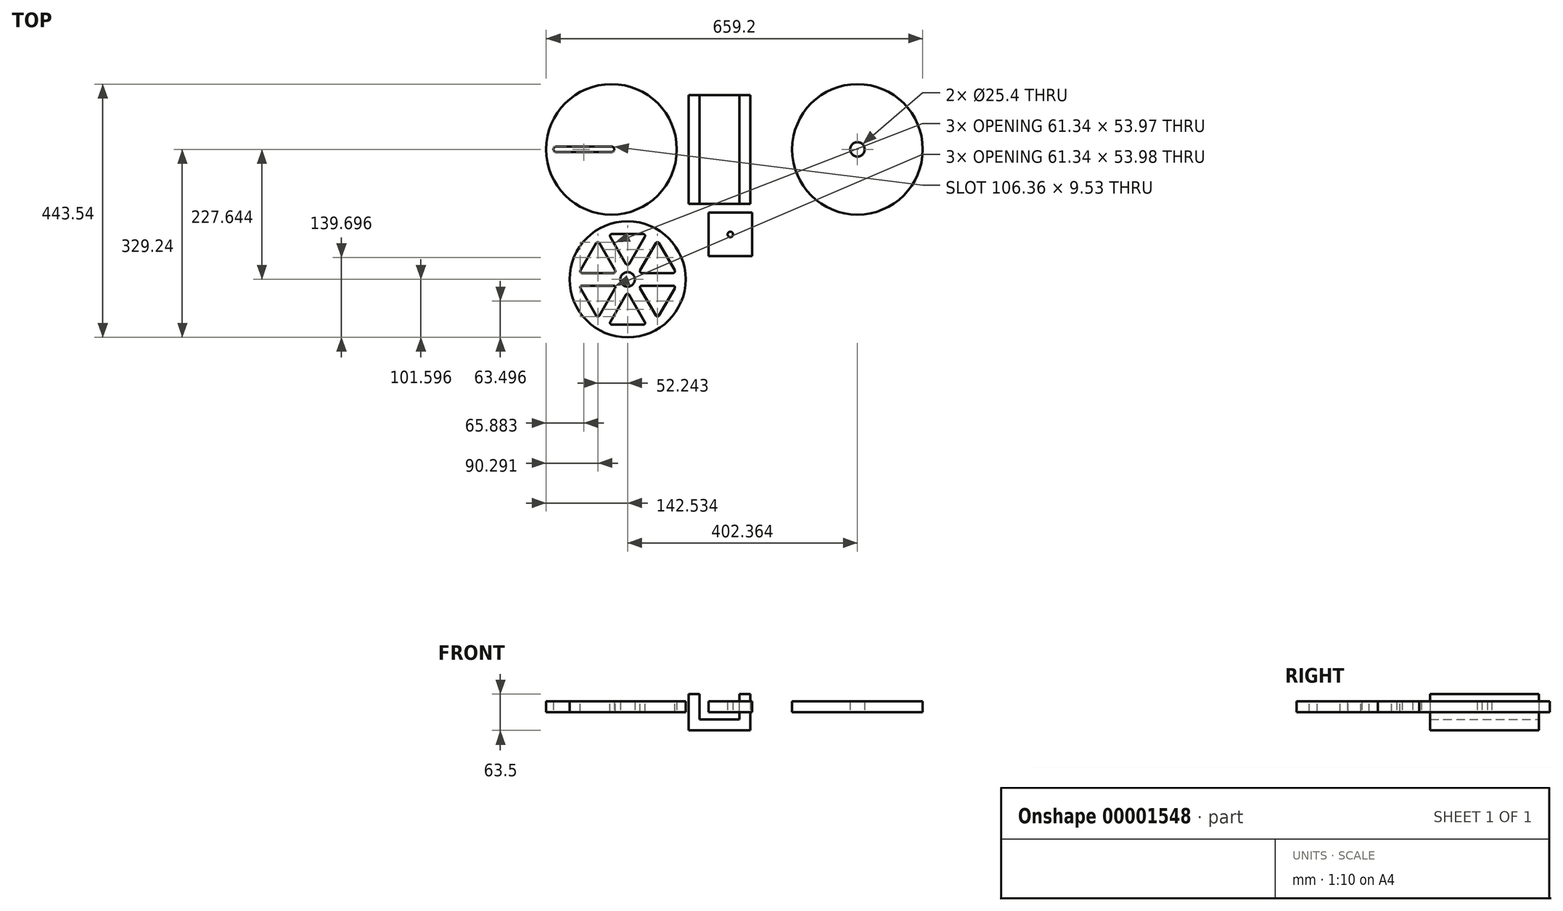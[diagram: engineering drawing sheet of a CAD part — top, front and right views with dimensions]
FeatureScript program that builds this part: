
annotation { "Feature Type Name" : "Feature", "Feature Type Description" : "" }
export const myFeature = defineFeature(function(context is Context, id is Id, definition is map)
    precondition{}
    {
        {
            var Q0;
            Q0=qCreatedBy(makeId("Front.planeOp"),FACE);
            var sketch = newSketch(context, id + "F0", { "sketchPlane" : qUnion([Q0])});
            skLineSegment(sketch, "E0.bottom", {"start": v(-53.98, 31.75) * mm, "end": v(-34.92, 31.75) * mm});
            skLineSegment(sketch, "E0.top", {"start": v(-53.97, -31.75) * mm, "end": v(53.98, -31.75) * mm});
            skLineSegment(sketch, "E0.left", {"start": v(-53.98, 31.75) * mm, "end": v(-53.98, -31.75) * mm});
            skLineSegment(sketch, "E0.right", {"start": v(53.98, 31.75) * mm, "end": v(53.98, -31.75) * mm});
            skLineSegment(sketch, "E1.0", {"start": v(-34.92, 12.7) * mm, "end": v(-34.92, -12.7) * mm});
            skLineSegment(sketch, "E1.2", {"start": v(34.93, 12.7) * mm, "end": v(34.93, -12.7) * mm});
            skLineSegment(sketch, "E1.3", {"start": v(-34.92, -12.7) * mm, "end": v(34.93, -12.7) * mm});
            skLineSegment(sketch, "E2", {"start": v(-34.92, 12.7) * mm, "end": v(-34.92, 31.75) * mm});
            skLineSegment(sketch, "E3", {"start": v(34.93, 12.7) * mm, "end": v(34.93, 31.75) * mm});
            skLineSegment(sketch, "E4.trimOffspring", {"start": v(34.93, 31.75) * mm, "end": v(53.98, 31.75) * mm});
            skSolve(sketch);
        }
        {
            var Q0;
            Q0=makeQuery(id+"F0.imprint","IMPRINT",FACE,{"disambiguationData":[TD([[makeQuery(id+"F0.imprint","IMPRINT",EDGE,{"derivedFrom":sQuery(id+"F0.wireOp",EDGE,"E0.bottom")}),-1.0]])]});
            extrude(context, id + "F1", {"entities" : qUnion([Q0]), "endBound" : BoundingType.SYMMETRIC, "depth" : 190.5 * mm});
        }
        {
            var Q0;
            Q0=qCreatedBy(makeId("Top.planeOp"),FACE);
            var sketch = newSketch(context, id + "F2", { "sketchPlane" : qUnion([Q0])});
            skCircle(sketch, "E5", {"center": v(241.4, 0) * mm, "radius": 114.3 * mm});
            skCircle(sketch, "E6", {"center": v(-189.19, 0) * mm, "radius": 114.3 * mm});
            skCircle(sketch, "E7", {"center": v(241.4, 0) * mm, "radius": 12.7 * mm});
            skArc(sketch, "E8", {"start": v(-189.19, -4.76) * mm, "mid": v(-184.43, 0) * mm, "end": v(-189.19, 4.76) * mm});
            skArc(sketch, "E9", {"start": v(-286.03, 4.76) * mm, "mid": v(-290.79, 0) * mm, "end": v(-286.03, -4.76) * mm});
            skLineSegment(sketch, "E10", {"start": v(-286.03, 4.76) * mm, "end": v(-189.19, 4.76) * mm});
            skLineSegment(sketch, "E11", {"start": v(-189.19, -4.76) * mm, "end": v(-286.03, -4.76) * mm});
            skLineSegment(sketch, "E12.bottom", {"start": v(-19.25, -110.9) * mm, "end": v(56.95, -110.9) * mm});
            skLineSegment(sketch, "E12.top", {"start": v(-19.25, -187.1) * mm, "end": v(56.95, -187.1) * mm});
            skLineSegment(sketch, "E12.left", {"start": v(-19.25, -110.9) * mm, "end": v(-19.25, -187.1) * mm});
            skLineSegment(sketch, "E12.right", {"start": v(56.95, -110.9) * mm, "end": v(56.95, -187.1) * mm});
            skCircle(sketch, "E13", {"center": v(18.85, -149) * mm, "radius": 4.76 * mm});
            skCircle(sketch, "E14", {"center": v(-160.96, -227.64) * mm, "radius": 101.6 * mm});
            skCircle(sketch, "E15", {"center": v(-160.96, -227.64) * mm, "radius": 12.7 * mm});
            skSolve(sketch);
        }
        {
            var Q0;
            {Q0=qUnion([makeQuery(id+"F2.imprint","IMPRINT",FACE,{"disambiguationData":[TD([[makeQuery(id+"F2.imprint","IMPRINT",EDGE,{"derivedFrom":sQuery(id+"F2.wireOp",EDGE,"E5")}),1.0]])]}),makeQuery(id+"F2.imprint","IMPRINT",FACE,{"disambiguationData":[TD([[makeQuery(id+"F2.imprint","IMPRINT",EDGE,{"derivedFrom":sQuery(id+"F2.wireOp",EDGE,"E6")}),1.0]])]}),makeQuery(id+"F2.imprint","IMPRINT",FACE,{"disambiguationData":[TD([[makeQuery(id+"F2.imprint","IMPRINT",EDGE,{"derivedFrom":sQuery(id+"F2.wireOp",EDGE,"E12.bottom")}),-1.0]])]}),makeQuery(id+"F2.imprint","IMPRINT",FACE,{"disambiguationData":[TD([[makeQuery(id+"F2.imprint","IMPRINT",EDGE,{"derivedFrom":sQuery(id+"F2.wireOp",EDGE,"E14")}),1.0]])]})]);}
            extrude(context, id + "F3", {"entities" : qUnion([Q0]), "depth" : 19.05 * mm});
        }
        {
            var Q0;
            Q0=makeQuery(id+"F3.opExtrude","CAP_FACE",FACE,{"disambiguationData":[OSD([sQuery(id+"F2.wireOp",EDGE,"E14"),sQuery(id+"F2.wireOp",EDGE,"E15")])],"isStart":false});
            var sketch = newSketch(context, id + "F4", { "sketchPlane" : qUnion([Q0])});
            skLineSegment(sketch, "E16", {"start": v(-160.96, -227.64) * mm, "end": v(-160.96, -126.04) * mm, "construction": true});
            skLineSegment(sketch, "E17", {"start": v(-160.96, -227.64) * mm, "end": v(-59.36, -227.64) * mm});
            skCircle(sketch, "E18.cCircle", {"center": v(-160.96, -167.32) * mm, "radius": 19.05 * mm, "construction": true});
            skLineSegment(sketch, "E18.0", {"start": v(-188.45, -148.27) * mm, "end": v(-133.46, -148.27) * mm});
            skLineSegment(sketch, "E18.1", {"start": v(-130.71, -153.03) * mm, "end": v(-158.2, -200.66) * mm});
            skLineSegment(sketch, "E18.2", {"start": v(-163.7, -200.66) * mm, "end": v(-191.2, -153.03) * mm});
            skPoint(sketch, "E18.0.midPoint", {"position": v(-160.96, -148.27) * mm});
            skPoint(sketch, "E19.visualSharp", {"position": v(-193.95, -148.27) * mm});
            skArc(sketch, "E19.filletArc", {"start": v(-188.45, -148.27) * mm, "mid": v(-191.2, -149.86) * mm, "end": v(-191.2, -153.03) * mm});
            skPoint(sketch, "E20.visualSharp", {"position": v(-160.96, -205.42) * mm});
            skArc(sketch, "E20.filletArc", {"start": v(-163.7, -200.66) * mm, "mid": v(-160.96, -202.24) * mm, "end": v(-158.2, -200.66) * mm});
            skPoint(sketch, "E21.visualSharp", {"position": v(-127.96, -148.27) * mm});
            skArc(sketch, "E21.filletArc", {"start": v(-130.71, -153.03) * mm, "mid": v(-130.71, -149.86) * mm, "end": v(-133.46, -148.27) * mm});
            skSolve(sketch);
        }
        {
            var Q0;
            Q0=makeQuery(id+"F4.imprint","IMPRINT",FACE,{"disambiguationData":[TD([[makeQuery(id+"F4.imprint","IMPRINT",EDGE,{"derivedFrom":sQuery(id+"F4.wireOp",EDGE,"E18.0")}),-1.0]])]});
            extrude(context, id + "F5", {"entities" : qUnion([Q0]), "oppositeDirection" : true, "depth" : 19.05 * mm});
        }
        {
            var Q0;
            Q0=makeQuery(id+"F3.opExtrude","CAP_FACE",FACE,{"disambiguationData":[OSD([sQuery(id+"F2.wireOp",EDGE,"E14"),sQuery(id+"F2.wireOp",EDGE,"E15")])],"isStart":false});
            var Q1;
            Q1=makeQuery(id+"F5.opExtrude","SWEPT_BODY",BODY,{"disambiguationData":[OSD([sQuery(id+"F4.wireOp",EDGE,"E18.0"),sQuery(id+"F4.wireOp",EDGE,"E18.1"),sQuery(id+"F4.wireOp",EDGE,"E18.2"),sQuery(id+"F4.wireOp",EDGE,"E19.filletArc"),sQuery(id+"F4.wireOp",EDGE,"E20.filletArc"),sQuery(id+"F4.wireOp",EDGE,"E21.filletArc")])]});
            var Q2;
            Q2=makeQuery(id+"F3.opExtrude","CAP_EDGE",EDGE,{"disambiguationData":[OSD([sQuery(id+"F2.wireOp",EDGE,"E15")])],"isStart":false});
            circularPattern(context, id + "F6", {"entities" : qUnion([Q1]), "axis" : qUnion([Q2]), "angle" : 360 * degree, "instanceCount" : 6, "equalSpace" : true});
        }
        {
            var Q0;
            Q0=makeQuery(id+"F6.opPattern","COPY",BODY,{"derivedFrom":makeQuery(id+"F5.opExtrude","SWEPT_BODY",BODY,{"disambiguationData":[OSD([sQuery(id+"F4.wireOp",EDGE,"E18.0"),sQuery(id+"F4.wireOp",EDGE,"E18.1"),sQuery(id+"F4.wireOp",EDGE,"E18.2"),sQuery(id+"F4.wireOp",EDGE,"E19.filletArc"),sQuery(id+"F4.wireOp",EDGE,"E20.filletArc"),sQuery(id+"F4.wireOp",EDGE,"E21.filletArc")])]}),"instanceName":"1"});
            var Q1;
            Q1=makeQuery(id+"F5.opExtrude","SWEPT_BODY",BODY,{"disambiguationData":[OSD([sQuery(id+"F4.wireOp",EDGE,"E18.0"),sQuery(id+"F4.wireOp",EDGE,"E18.1"),sQuery(id+"F4.wireOp",EDGE,"E18.2"),sQuery(id+"F4.wireOp",EDGE,"E19.filletArc"),sQuery(id+"F4.wireOp",EDGE,"E20.filletArc"),sQuery(id+"F4.wireOp",EDGE,"E21.filletArc")])]});
            var Q2;
            Q2=makeQuery(id+"F6.opPattern","COPY",BODY,{"derivedFrom":makeQuery(id+"F5.opExtrude","SWEPT_BODY",BODY,{"disambiguationData":[OSD([sQuery(id+"F4.wireOp",EDGE,"E18.0"),sQuery(id+"F4.wireOp",EDGE,"E18.1"),sQuery(id+"F4.wireOp",EDGE,"E18.2"),sQuery(id+"F4.wireOp",EDGE,"E19.filletArc"),sQuery(id+"F4.wireOp",EDGE,"E20.filletArc"),sQuery(id+"F4.wireOp",EDGE,"E21.filletArc")])]}),"instanceName":"5"});
            var Q3;
            Q3=makeQuery(id+"F6.opPattern","COPY",BODY,{"derivedFrom":makeQuery(id+"F5.opExtrude","SWEPT_BODY",BODY,{"disambiguationData":[OSD([sQuery(id+"F4.wireOp",EDGE,"E18.0"),sQuery(id+"F4.wireOp",EDGE,"E18.1"),sQuery(id+"F4.wireOp",EDGE,"E18.2"),sQuery(id+"F4.wireOp",EDGE,"E19.filletArc"),sQuery(id+"F4.wireOp",EDGE,"E20.filletArc"),sQuery(id+"F4.wireOp",EDGE,"E21.filletArc")])]}),"instanceName":"4"});
            var Q4;
            Q4=makeQuery(id+"F6.opPattern","COPY",BODY,{"derivedFrom":makeQuery(id+"F5.opExtrude","SWEPT_BODY",BODY,{"disambiguationData":[OSD([sQuery(id+"F4.wireOp",EDGE,"E18.0"),sQuery(id+"F4.wireOp",EDGE,"E18.1"),sQuery(id+"F4.wireOp",EDGE,"E18.2"),sQuery(id+"F4.wireOp",EDGE,"E19.filletArc"),sQuery(id+"F4.wireOp",EDGE,"E20.filletArc"),sQuery(id+"F4.wireOp",EDGE,"E21.filletArc")])]}),"instanceName":"3"});
            var Q5;
            Q5=makeQuery(id+"F6.opPattern","COPY",BODY,{"derivedFrom":makeQuery(id+"F5.opExtrude","SWEPT_BODY",BODY,{"disambiguationData":[OSD([sQuery(id+"F4.wireOp",EDGE,"E18.0"),sQuery(id+"F4.wireOp",EDGE,"E18.1"),sQuery(id+"F4.wireOp",EDGE,"E18.2"),sQuery(id+"F4.wireOp",EDGE,"E19.filletArc"),sQuery(id+"F4.wireOp",EDGE,"E20.filletArc"),sQuery(id+"F4.wireOp",EDGE,"E21.filletArc")])]}),"instanceName":"2"});
            var Q6;
            Q6=makeQuery(id+"F3.opExtrude","SWEPT_BODY",BODY,{"disambiguationData":[OSD([sQuery(id+"F2.wireOp",EDGE,"E14"),sQuery(id+"F2.wireOp",EDGE,"E15")])]});
            booleanBodies(context, id + "F7", {"operationType" : BooleanOperationType.SUBTRACTION, "tools" : qUnion([Q0, Q1, Q2, Q3, Q4, Q5]), "targets" : qUnion([Q6])});
        }
    });
